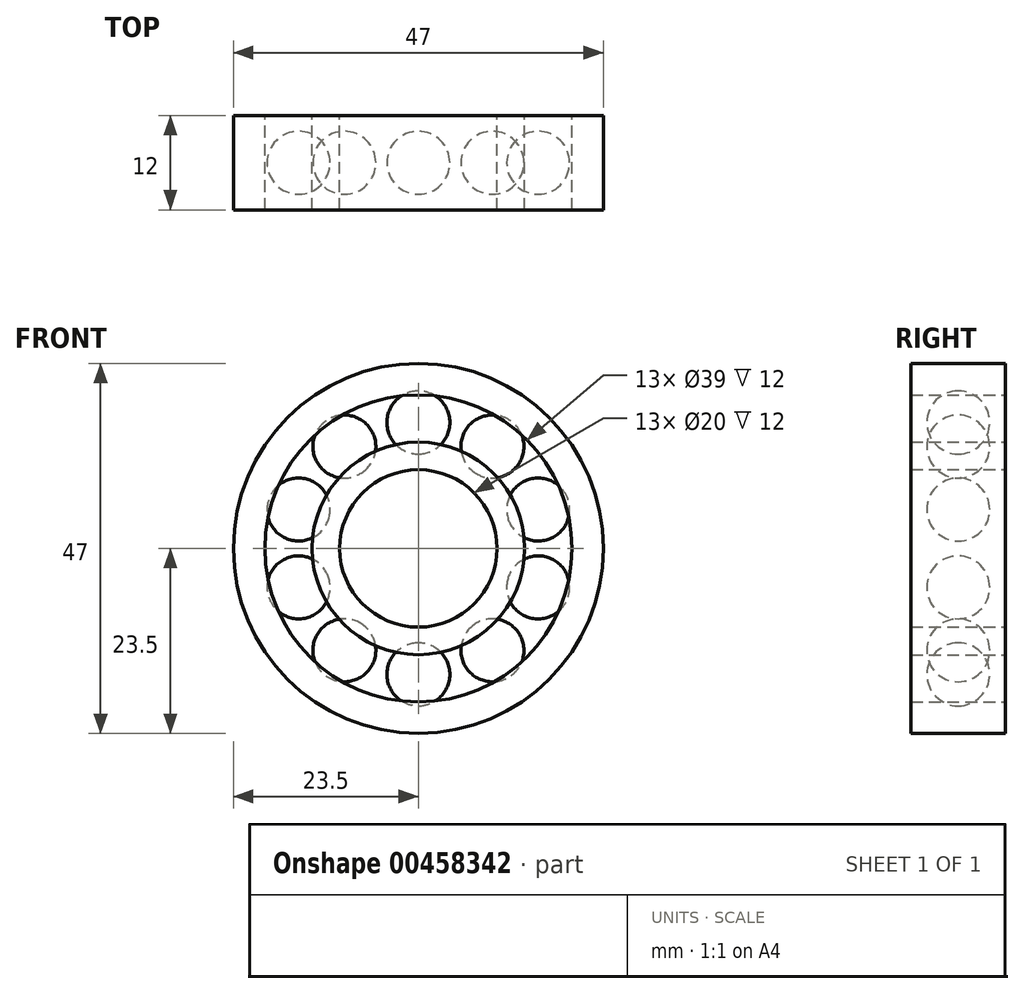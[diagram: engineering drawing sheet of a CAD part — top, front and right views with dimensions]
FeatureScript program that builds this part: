
annotation { "Feature Type Name" : "Feature", "Feature Type Description" : "" }
export const myFeature = defineFeature(function(context is Context, id is Id, definition is map)
    precondition{}
    {
        {
            var Q0;
            Q0=qCreatedBy(makeId("Front.planeOp"),FACE);
            var sketch = newSketch(context, id + "F0", { "sketchPlane" : qUnion([Q0])});
            skCircle(sketch, "E0", {"center": v(0, 0) * mm, "radius": 23.5 * mm});
            skCircle(sketch, "E1", {"center": v(0, 0) * mm, "radius": 19.5 * mm});
            skCircle(sketch, "E2", {"center": v(0, 0) * mm, "radius": 13.5 * mm});
            skCircle(sketch, "E3", {"center": v(0, 0) * mm, "radius": 10 * mm});
            skSolve(sketch);
        }
        {
            var Q0;
            Q0=makeQuery(id+"F0.imprint","IMPRINT",FACE,{"disambiguationData":[TD([[makeQuery(id+"F0.imprint","IMPRINT",EDGE,{"derivedFrom":sQuery(id+"F0.wireOp",EDGE,"E0")}),1.0]])]});
            var Q1;
            Q1=makeQuery(id+"F0.imprint","IMPRINT",FACE,{"disambiguationData":[TD([[makeQuery(id+"F0.imprint","IMPRINT",EDGE,{"derivedFrom":sQuery(id+"F0.wireOp",EDGE,"E2")}),1.0]])]});
            extrude(context, id + "F1", {"entities" : qUnion([Q0, Q1]), "depth" : 12 * mm});
        }
        {
            var Q0;
            Q0=qCreatedBy(makeId("Front.planeOp"),FACE);
            cPlane(context, id + "F2", {"entities" : qUnion([Q0]), "cplaneType" : CPlaneType.OFFSET, "offset" : 6 * mm, "width" : 150 * mm, "height" : 150 * mm});
        }
        {
            var Q0;
            Q0=qCreatedBy(id+"F2.planeOp",FACE);
            var sketch = newSketch(context, id + "F3", { "sketchPlane" : qUnion([Q0])});
            skArc(sketch, "E4", {"start": v(0, 4) * mm, "mid": v(-4, 0) * mm, "end": v(0, -4) * mm});
            skLineSegment(sketch, "E5", {"start": v(0, 0) * mm, "end": v(0, 4) * mm});
            skLineSegment(sketch, "E6", {"start": v(0, 4) * mm, "end": v(0, -4) * mm});
            skSolve(sketch);
        }
        {
            var Q0;
            {var subQ0=sQuery(id+"F3.wireOp",EDGE,"E4");Q0=makeQuery(id+"F3.imprint","IMPRINT",FACE,{"disambiguationData":[TD([[makeQuery(id+"F3.imprint","IMPRINT",EDGE,{"derivedFrom":subQ0}),1.0]])]});}
            var Q1;
            Q1=sQuery(id+"F3.wireOp",EDGE,"E6");
            revolve(context, id + "F4", {"entities" : qUnion([Q0]), "axis" : qUnion([Q1]), "revolveType" : RevolveType.FULL});
        }
        {
            var Q0;
            Q0=makeQuery(id+"F4.opRevolve","SWEPT_BODY",BODY,{"disambiguationData":[OSD([sQuery(id+"F3.wireOp",EDGE,"E4"),sQuery(id+"F3.wireOp",EDGE,"E6")])]});
            transform(context, id + "F5", {"entities" : qUnion([Q0]), "transformType" : TransformType.TRANSLATION_3D, "dx" : 0 * mm, "dy" : 0 * mm, "dz" : 16 * mm, "makeCopy" : false});
        }
        {
            var Q0;
            Q0=makeQuery(id+"F4.opRevolve","SWEPT_BODY",BODY,{"disambiguationData":[OSD([sQuery(id+"F3.wireOp",EDGE,"E4"),sQuery(id+"F3.wireOp",EDGE,"E6")])]});
            var Q1;
            Q1=makeQuery(id+"F1.opExtrude","SWEPT_FACE",FACE,{"disambiguationData":[OSD([sQuery(id+"F0.wireOp",EDGE,"E2")])]});
            circularPattern(context, id + "F6", {"entities" : qUnion([Q0]), "axis" : qUnion([Q1]), "angle" : 360 * degree, "instanceCount" : 10, "equalSpace" : true});
        }
    });
